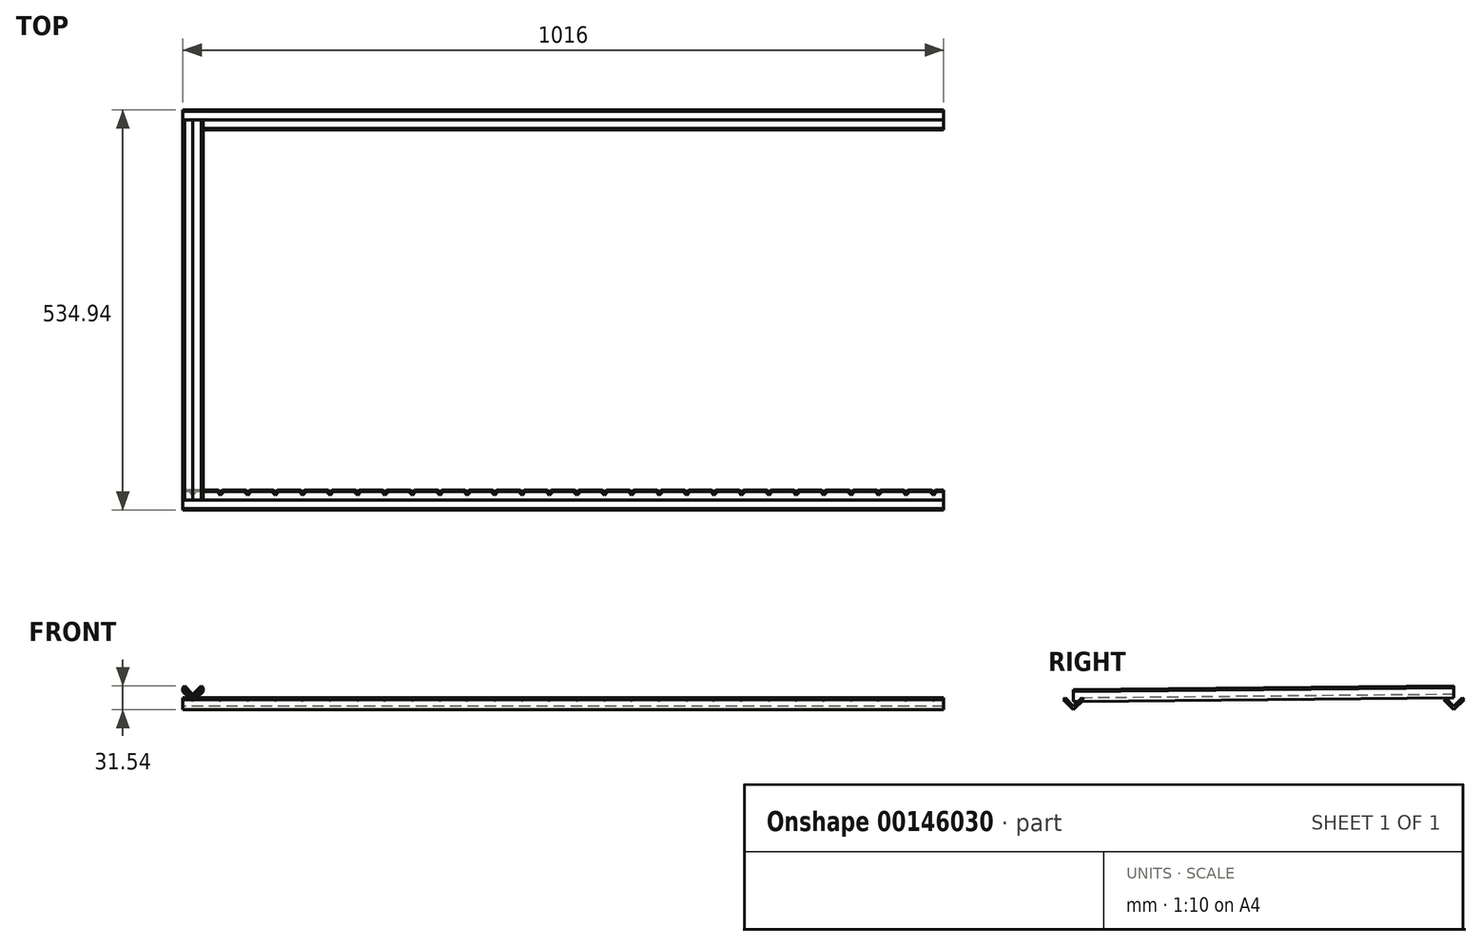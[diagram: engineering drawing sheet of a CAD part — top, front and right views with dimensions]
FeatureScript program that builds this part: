
annotation { "Feature Type Name" : "Feature", "Feature Type Description" : "" }
export const myFeature = defineFeature(function(context is Context, id is Id, definition is map)
    precondition{}
    {
        {
            var Q0;
            Q0=qCreatedBy(makeId("Right.planeOp"),FACE);
            var sketch = newSketch(context, id + "F0", { "sketchPlane" : qUnion([Q0])});
            skLineSegment(sketch, "E0", {"start": v(0, 0) * mm, "end": v(13.47, 13.47) * mm});
            skLineSegment(sketch, "E1", {"start": v(0, 0) * mm, "end": v(-13.47, 13.47) * mm});
            skLineSegment(sketch, "E2.0", {"start": v(0, 4.5) * mm, "end": v(-11.23, 15.72) * mm});
            skLineSegment(sketch, "E2.1", {"start": v(0, 4.5) * mm, "end": v(11.23, 15.72) * mm});
            skLineSegment(sketch, "E3", {"start": v(-13.47, 13.47) * mm, "end": v(-11.23, 15.72) * mm});
            skLineSegment(sketch, "E4", {"start": v(11.23, 15.72) * mm, "end": v(13.47, 13.47) * mm});
            skSolve(sketch);
        }
        {
            var Q0;
            Q0 = qSketchRegion(id + "F0", true);
            extrude(context, id + "F1", {"entities" : qUnion([Q0]), "depth" : 1016 * mm});
        }
        {
            var Q0;
            Q0=makeQuery(id+"F1.opExtrude","SWEPT_BODY",BODY,{"disambiguationData":[OSD([sQuery(id+"F0.wireOp",EDGE,"E0"),sQuery(id+"F0.wireOp",EDGE,"E1"),sQuery(id+"F0.wireOp",EDGE,"E2.0"),sQuery(id+"F0.wireOp",EDGE,"E2.1"),sQuery(id+"F0.wireOp",EDGE,"E3"),sQuery(id+"F0.wireOp",EDGE,"E4")])]});
            transform(context, id + "F2", {"entities" : qUnion([Q0]), "transformType" : TransformType.TRANSLATION_3D, "dx" : 0 * mm, "dy" : 508 * mm, "dz" : 0 * mm, "makeCopy" : true});
        }
        {
            var Q0;
            Q0=qCreatedBy(makeId("Front.planeOp"),FACE);
            var sketch = newSketch(context, id + "F3", { "sketchPlane" : qUnion([Q0])});
            skLineSegment(sketch, "E5.0", {"start": v(1016, 15.72) * mm, "end": v(0, 15.72) * mm});
            skLineSegment(sketch, "E6", {"start": v(13.47, 10.95) * mm, "end": v(26.94, 24.42) * mm});
            skLineSegment(sketch, "E7", {"start": v(13.47, 10.95) * mm, "end": v(0, 24.42) * mm});
            skLineSegment(sketch, "E8", {"start": v(0, 24.42) * mm, "end": v(2.25, 26.67) * mm});
            skLineSegment(sketch, "E9", {"start": v(24.7, 26.67) * mm, "end": v(26.94, 24.42) * mm});
            skPoint(sketch, "E10.endSnap0", {"position": v(1.12, 25.55) * mm});
            skLineSegment(sketch, "E11", {"start": v(2.25, 26.67) * mm, "end": v(24.7, 26.67) * mm});
            skLineSegment(sketch, "E12.1.0.0", {"start": v(38.87, 26.67) * mm, "end": v(61.32, 26.67) * mm});
            skPoint(sketch, "E12.1.0.1", {"position": v(37.75, 25.55) * mm});
            skLineSegment(sketch, "E12.1.0.2", {"start": v(50.1, 10.95) * mm, "end": v(36.63, 24.42) * mm});
            skLineSegment(sketch, "E12.1.0.3", {"start": v(50.1, 10.95) * mm, "end": v(63.57, 24.42) * mm});
            skLineSegment(sketch, "E12.1.0.4", {"start": v(61.32, 26.67) * mm, "end": v(63.57, 24.42) * mm});
            skLineSegment(sketch, "E12.1.0.5", {"start": v(36.63, 24.42) * mm, "end": v(38.87, 26.67) * mm});
            skLineSegment(sketch, "E12.2.0.0", {"start": v(75.5, 26.67) * mm, "end": v(97.95, 26.67) * mm});
            skPoint(sketch, "E12.2.0.1", {"position": v(74.38, 25.55) * mm});
            skLineSegment(sketch, "E12.2.0.2", {"start": v(86.72, 10.95) * mm, "end": v(73.25, 24.42) * mm});
            skLineSegment(sketch, "E12.2.0.3", {"start": v(86.72, 10.95) * mm, "end": v(100.2, 24.42) * mm});
            skLineSegment(sketch, "E12.2.0.4", {"start": v(97.95, 26.67) * mm, "end": v(100.2, 24.42) * mm});
            skLineSegment(sketch, "E12.2.0.5", {"start": v(73.25, 24.42) * mm, "end": v(75.5, 26.67) * mm});
            skLineSegment(sketch, "E12.direction1", {"start": v(13.47, 10.95) * mm, "end": v(50.1, 10.95) * mm, "construction": true});
            skLineSegment(sketch, "E13.0.3.0", {"start": v(112.13, 26.67) * mm, "end": v(134.58, 26.67) * mm});
            skPoint(sketch, "E13.3.3.0", {"position": v(111, 25.55) * mm});
            skLineSegment(sketch, "E13.4.3.0", {"start": v(123.35, 10.95) * mm, "end": v(109.88, 24.42) * mm});
            skLineSegment(sketch, "E13.7.3.0", {"start": v(123.35, 10.95) * mm, "end": v(136.82, 24.42) * mm});
            skLineSegment(sketch, "E13.10.3.0", {"start": v(134.58, 26.67) * mm, "end": v(136.82, 24.42) * mm});
            skLineSegment(sketch, "E13.13.3.0", {"start": v(109.88, 24.42) * mm, "end": v(112.13, 26.67) * mm});
            skLineSegment(sketch, "E13.0.4.0", {"start": v(148.75, 26.67) * mm, "end": v(171.2, 26.67) * mm});
            skPoint(sketch, "E13.3.4.0", {"position": v(147.63, 25.55) * mm});
            skLineSegment(sketch, "E13.4.4.0", {"start": v(159.98, 10.95) * mm, "end": v(146.5, 24.42) * mm});
            skLineSegment(sketch, "E13.7.4.0", {"start": v(159.98, 10.95) * mm, "end": v(173.45, 24.42) * mm});
            skLineSegment(sketch, "E13.10.4.0", {"start": v(171.2, 26.67) * mm, "end": v(173.45, 24.42) * mm});
            skLineSegment(sketch, "E13.13.4.0", {"start": v(146.5, 24.42) * mm, "end": v(148.75, 26.67) * mm});
            skLineSegment(sketch, "E13.0.5.0", {"start": v(185.38, 26.67) * mm, "end": v(207.83, 26.67) * mm});
            skPoint(sketch, "E13.3.5.0", {"position": v(184.26, 25.55) * mm});
            skLineSegment(sketch, "E13.4.5.0", {"start": v(196.6, 10.95) * mm, "end": v(183.13, 24.42) * mm});
            skLineSegment(sketch, "E13.7.5.0", {"start": v(196.6, 10.95) * mm, "end": v(210.08, 24.42) * mm});
            skLineSegment(sketch, "E13.10.5.0", {"start": v(207.83, 26.67) * mm, "end": v(210.08, 24.42) * mm});
            skLineSegment(sketch, "E13.13.5.0", {"start": v(183.13, 24.42) * mm, "end": v(185.38, 26.67) * mm});
            skLineSegment(sketch, "E13.0.6.0", {"start": v(222, 26.67) * mm, "end": v(244.46, 26.67) * mm});
            skPoint(sketch, "E13.3.6.0", {"position": v(220.88, 25.55) * mm});
            skLineSegment(sketch, "E13.4.6.0", {"start": v(233.23, 10.95) * mm, "end": v(219.76, 24.42) * mm});
            skLineSegment(sketch, "E13.7.6.0", {"start": v(233.23, 10.95) * mm, "end": v(246.7, 24.42) * mm});
            skLineSegment(sketch, "E13.10.6.0", {"start": v(244.46, 26.67) * mm, "end": v(246.7, 24.42) * mm});
            skLineSegment(sketch, "E13.13.6.0", {"start": v(219.76, 24.42) * mm, "end": v(222, 26.67) * mm});
            skLineSegment(sketch, "E13.0.7.0", {"start": v(258.63, 26.67) * mm, "end": v(281.08, 26.67) * mm});
            skPoint(sketch, "E13.3.7.0", {"position": v(257.51, 25.55) * mm});
            skLineSegment(sketch, "E13.4.7.0", {"start": v(269.86, 10.95) * mm, "end": v(256.39, 24.42) * mm});
            skLineSegment(sketch, "E13.7.7.0", {"start": v(269.86, 10.95) * mm, "end": v(283.33, 24.42) * mm});
            skLineSegment(sketch, "E13.10.7.0", {"start": v(281.08, 26.67) * mm, "end": v(283.33, 24.42) * mm});
            skLineSegment(sketch, "E13.13.7.0", {"start": v(256.39, 24.42) * mm, "end": v(258.63, 26.67) * mm});
            skLineSegment(sketch, "E13.0.8.0", {"start": v(295.26, 26.67) * mm, "end": v(317.71, 26.67) * mm});
            skPoint(sketch, "E13.3.8.0", {"position": v(294.14, 25.55) * mm});
            skLineSegment(sketch, "E13.4.8.0", {"start": v(306.49, 10.95) * mm, "end": v(293.01, 24.42) * mm});
            skLineSegment(sketch, "E13.7.8.0", {"start": v(306.49, 10.95) * mm, "end": v(319.96, 24.42) * mm});
            skLineSegment(sketch, "E13.10.8.0", {"start": v(317.71, 26.67) * mm, "end": v(319.96, 24.42) * mm});
            skLineSegment(sketch, "E13.13.8.0", {"start": v(293.01, 24.42) * mm, "end": v(295.26, 26.67) * mm});
            skLineSegment(sketch, "E13.0.9.0", {"start": v(331.89, 26.67) * mm, "end": v(354.34, 26.67) * mm});
            skPoint(sketch, "E13.3.9.0", {"position": v(330.76, 25.55) * mm});
            skLineSegment(sketch, "E13.4.9.0", {"start": v(343.11, 10.95) * mm, "end": v(329.64, 24.42) * mm});
            skLineSegment(sketch, "E13.7.9.0", {"start": v(343.11, 10.95) * mm, "end": v(356.58, 24.42) * mm});
            skLineSegment(sketch, "E13.10.9.0", {"start": v(354.34, 26.67) * mm, "end": v(356.58, 24.42) * mm});
            skLineSegment(sketch, "E13.13.9.0", {"start": v(329.64, 24.42) * mm, "end": v(331.89, 26.67) * mm});
            skLineSegment(sketch, "E13.0.10.0", {"start": v(368.51, 26.67) * mm, "end": v(390.96, 26.67) * mm});
            skPoint(sketch, "E13.3.10.0", {"position": v(367.4, 25.55) * mm});
            skLineSegment(sketch, "E13.4.10.0", {"start": v(379.74, 10.95) * mm, "end": v(366.27, 24.42) * mm});
            skLineSegment(sketch, "E13.7.10.0", {"start": v(379.74, 10.95) * mm, "end": v(393.2, 24.42) * mm});
            skLineSegment(sketch, "E13.10.10.0", {"start": v(390.96, 26.67) * mm, "end": v(393.2, 24.42) * mm});
            skLineSegment(sketch, "E13.13.10.0", {"start": v(366.27, 24.42) * mm, "end": v(368.51, 26.67) * mm});
            skLineSegment(sketch, "E13.0.11.0", {"start": v(405.14, 26.67) * mm, "end": v(427.6, 26.67) * mm});
            skPoint(sketch, "E13.3.11.0", {"position": v(404.02, 25.55) * mm});
            skLineSegment(sketch, "E13.4.11.0", {"start": v(416.37, 10.95) * mm, "end": v(402.9, 24.42) * mm});
            skLineSegment(sketch, "E13.7.11.0", {"start": v(416.37, 10.95) * mm, "end": v(429.84, 24.42) * mm});
            skLineSegment(sketch, "E13.10.11.0", {"start": v(427.6, 26.67) * mm, "end": v(429.84, 24.42) * mm});
            skLineSegment(sketch, "E13.13.11.0", {"start": v(402.9, 24.42) * mm, "end": v(405.14, 26.67) * mm});
            skLineSegment(sketch, "E13.0.12.0", {"start": v(441.77, 26.67) * mm, "end": v(464.22, 26.67) * mm});
            skPoint(sketch, "E13.3.12.0", {"position": v(440.64, 25.55) * mm});
            skLineSegment(sketch, "E13.4.12.0", {"start": v(453, 10.95) * mm, "end": v(439.52, 24.42) * mm});
            skLineSegment(sketch, "E13.7.12.0", {"start": v(453, 10.95) * mm, "end": v(466.46, 24.42) * mm});
            skLineSegment(sketch, "E13.10.12.0", {"start": v(464.22, 26.67) * mm, "end": v(466.46, 24.42) * mm});
            skLineSegment(sketch, "E13.13.12.0", {"start": v(439.52, 24.42) * mm, "end": v(441.77, 26.67) * mm});
            skLineSegment(sketch, "E13.0.13.0", {"start": v(478.4, 26.67) * mm, "end": v(500.84, 26.67) * mm});
            skPoint(sketch, "E13.3.13.0", {"position": v(477.27, 25.55) * mm});
            skLineSegment(sketch, "E13.4.13.0", {"start": v(489.62, 10.95) * mm, "end": v(476.15, 24.42) * mm});
            skLineSegment(sketch, "E13.7.13.0", {"start": v(489.62, 10.95) * mm, "end": v(503.09, 24.42) * mm});
            skLineSegment(sketch, "E13.10.13.0", {"start": v(500.84, 26.67) * mm, "end": v(503.09, 24.42) * mm});
            skLineSegment(sketch, "E13.13.13.0", {"start": v(476.15, 24.42) * mm, "end": v(478.4, 26.67) * mm});
            skLineSegment(sketch, "E13.0.14.0", {"start": v(515.02, 26.67) * mm, "end": v(537.47, 26.67) * mm});
            skPoint(sketch, "E13.3.14.0", {"position": v(513.9, 25.55) * mm});
            skLineSegment(sketch, "E13.4.14.0", {"start": v(526.25, 10.95) * mm, "end": v(512.78, 24.42) * mm});
            skLineSegment(sketch, "E13.7.14.0", {"start": v(526.25, 10.95) * mm, "end": v(539.72, 24.42) * mm});
            skLineSegment(sketch, "E13.10.14.0", {"start": v(537.47, 26.67) * mm, "end": v(539.72, 24.42) * mm});
            skLineSegment(sketch, "E13.13.14.0", {"start": v(512.78, 24.42) * mm, "end": v(515.02, 26.67) * mm});
            skLineSegment(sketch, "E13.0.15.0", {"start": v(551.65, 26.67) * mm, "end": v(574.1, 26.67) * mm});
            skPoint(sketch, "E13.3.15.0", {"position": v(550.53, 25.55) * mm});
            skLineSegment(sketch, "E13.4.15.0", {"start": v(562.87, 10.95) * mm, "end": v(549.4, 24.42) * mm});
            skLineSegment(sketch, "E13.7.15.0", {"start": v(562.87, 10.95) * mm, "end": v(576.34, 24.42) * mm});
            skLineSegment(sketch, "E13.10.15.0", {"start": v(574.1, 26.67) * mm, "end": v(576.34, 24.42) * mm});
            skLineSegment(sketch, "E13.13.15.0", {"start": v(549.4, 24.42) * mm, "end": v(551.65, 26.67) * mm});
            skLineSegment(sketch, "E13.0.16.0", {"start": v(588.27, 26.67) * mm, "end": v(610.73, 26.67) * mm});
            skPoint(sketch, "E13.3.16.0", {"position": v(587.15, 25.55) * mm});
            skLineSegment(sketch, "E13.4.16.0", {"start": v(599.5, 10.95) * mm, "end": v(586.03, 24.42) * mm});
            skLineSegment(sketch, "E13.7.16.0", {"start": v(599.5, 10.95) * mm, "end": v(612.97, 24.42) * mm});
            skLineSegment(sketch, "E13.10.16.0", {"start": v(610.73, 26.67) * mm, "end": v(612.97, 24.42) * mm});
            skLineSegment(sketch, "E13.13.16.0", {"start": v(586.03, 24.42) * mm, "end": v(588.27, 26.67) * mm});
            skLineSegment(sketch, "E13.0.17.0", {"start": v(624.9, 26.67) * mm, "end": v(647.35, 26.67) * mm});
            skPoint(sketch, "E13.3.17.0", {"position": v(623.78, 25.55) * mm});
            skLineSegment(sketch, "E13.4.17.0", {"start": v(636.13, 10.95) * mm, "end": v(622.66, 24.42) * mm});
            skLineSegment(sketch, "E13.7.17.0", {"start": v(636.13, 10.95) * mm, "end": v(649.6, 24.42) * mm});
            skLineSegment(sketch, "E13.10.17.0", {"start": v(647.35, 26.67) * mm, "end": v(649.6, 24.42) * mm});
            skLineSegment(sketch, "E13.13.17.0", {"start": v(622.66, 24.42) * mm, "end": v(624.9, 26.67) * mm});
            skLineSegment(sketch, "E13.0.18.0", {"start": v(661.53, 26.67) * mm, "end": v(683.98, 26.67) * mm});
            skPoint(sketch, "E13.3.18.0", {"position": v(660.4, 25.55) * mm});
            skLineSegment(sketch, "E13.4.18.0", {"start": v(672.75, 10.95) * mm, "end": v(659.28, 24.42) * mm});
            skLineSegment(sketch, "E13.7.18.0", {"start": v(672.75, 10.95) * mm, "end": v(686.22, 24.42) * mm});
            skLineSegment(sketch, "E13.10.18.0", {"start": v(683.98, 26.67) * mm, "end": v(686.22, 24.42) * mm});
            skLineSegment(sketch, "E13.13.18.0", {"start": v(659.28, 24.42) * mm, "end": v(661.53, 26.67) * mm});
            skLineSegment(sketch, "E13.0.19.0", {"start": v(698.15, 26.67) * mm, "end": v(720.6, 26.67) * mm});
            skPoint(sketch, "E13.3.19.0", {"position": v(697.03, 25.55) * mm});
            skLineSegment(sketch, "E13.4.19.0", {"start": v(709.38, 10.95) * mm, "end": v(695.9, 24.42) * mm});
            skLineSegment(sketch, "E13.7.19.0", {"start": v(709.38, 10.95) * mm, "end": v(722.85, 24.42) * mm});
            skLineSegment(sketch, "E13.10.19.0", {"start": v(720.6, 26.67) * mm, "end": v(722.85, 24.42) * mm});
            skLineSegment(sketch, "E13.13.19.0", {"start": v(695.9, 24.42) * mm, "end": v(698.15, 26.67) * mm});
            skLineSegment(sketch, "E14.0.20.0", {"start": v(734.78, 26.67) * mm, "end": v(757.23, 26.67) * mm});
            skPoint(sketch, "E14.3.20.0", {"position": v(733.66, 25.55) * mm});
            skLineSegment(sketch, "E14.4.20.0", {"start": v(746, 10.95) * mm, "end": v(732.54, 24.42) * mm});
            skLineSegment(sketch, "E14.7.20.0", {"start": v(746, 10.95) * mm, "end": v(759.48, 24.42) * mm});
            skLineSegment(sketch, "E14.10.20.0", {"start": v(757.23, 26.67) * mm, "end": v(759.48, 24.42) * mm});
            skLineSegment(sketch, "E14.13.20.0", {"start": v(732.54, 24.42) * mm, "end": v(734.78, 26.67) * mm});
            skLineSegment(sketch, "E14.0.21.0", {"start": v(771.4, 26.67) * mm, "end": v(793.86, 26.67) * mm});
            skPoint(sketch, "E14.3.21.0", {"position": v(770.29, 25.55) * mm});
            skLineSegment(sketch, "E14.4.21.0", {"start": v(782.63, 10.95) * mm, "end": v(769.16, 24.42) * mm});
            skLineSegment(sketch, "E14.7.21.0", {"start": v(782.63, 10.95) * mm, "end": v(796.1, 24.42) * mm});
            skLineSegment(sketch, "E14.10.21.0", {"start": v(793.86, 26.67) * mm, "end": v(796.1, 24.42) * mm});
            skLineSegment(sketch, "E14.13.21.0", {"start": v(769.16, 24.42) * mm, "end": v(771.4, 26.67) * mm});
            skLineSegment(sketch, "E14.0.22.0", {"start": v(808.04, 26.67) * mm, "end": v(830.49, 26.67) * mm});
            skPoint(sketch, "E14.3.22.0", {"position": v(806.91, 25.55) * mm});
            skLineSegment(sketch, "E14.4.22.0", {"start": v(819.26, 10.95) * mm, "end": v(805.8, 24.42) * mm});
            skLineSegment(sketch, "E14.7.22.0", {"start": v(819.26, 10.95) * mm, "end": v(832.73, 24.42) * mm});
            skLineSegment(sketch, "E14.10.22.0", {"start": v(830.49, 26.67) * mm, "end": v(832.73, 24.42) * mm});
            skLineSegment(sketch, "E14.13.22.0", {"start": v(805.8, 24.42) * mm, "end": v(808.04, 26.67) * mm});
            skLineSegment(sketch, "E14.0.23.0", {"start": v(844.66, 26.67) * mm, "end": v(867.11, 26.67) * mm});
            skPoint(sketch, "E14.3.23.0", {"position": v(843.54, 25.55) * mm});
            skLineSegment(sketch, "E14.4.23.0", {"start": v(855.89, 10.95) * mm, "end": v(842.42, 24.42) * mm});
            skLineSegment(sketch, "E14.7.23.0", {"start": v(855.89, 10.95) * mm, "end": v(869.36, 24.42) * mm});
            skLineSegment(sketch, "E14.10.23.0", {"start": v(867.11, 26.67) * mm, "end": v(869.36, 24.42) * mm});
            skLineSegment(sketch, "E14.13.23.0", {"start": v(842.42, 24.42) * mm, "end": v(844.66, 26.67) * mm});
            skLineSegment(sketch, "E14.0.24.0", {"start": v(881.29, 26.67) * mm, "end": v(903.74, 26.67) * mm});
            skPoint(sketch, "E14.3.24.0", {"position": v(880.17, 25.55) * mm});
            skLineSegment(sketch, "E14.4.24.0", {"start": v(892.51, 10.95) * mm, "end": v(879.04, 24.42) * mm});
            skLineSegment(sketch, "E14.7.24.0", {"start": v(892.51, 10.95) * mm, "end": v(905.98, 24.42) * mm});
            skLineSegment(sketch, "E14.10.24.0", {"start": v(903.74, 26.67) * mm, "end": v(905.98, 24.42) * mm});
            skLineSegment(sketch, "E14.13.24.0", {"start": v(879.04, 24.42) * mm, "end": v(881.29, 26.67) * mm});
            skLineSegment(sketch, "E14.0.25.0", {"start": v(917.92, 26.67) * mm, "end": v(940.37, 26.67) * mm});
            skPoint(sketch, "E14.3.25.0", {"position": v(916.8, 25.55) * mm});
            skLineSegment(sketch, "E14.4.25.0", {"start": v(929.14, 10.95) * mm, "end": v(915.67, 24.42) * mm});
            skLineSegment(sketch, "E14.7.25.0", {"start": v(929.14, 10.95) * mm, "end": v(942.61, 24.42) * mm});
            skLineSegment(sketch, "E14.10.25.0", {"start": v(940.37, 26.67) * mm, "end": v(942.61, 24.42) * mm});
            skLineSegment(sketch, "E14.13.25.0", {"start": v(915.67, 24.42) * mm, "end": v(917.92, 26.67) * mm});
            skLineSegment(sketch, "E14.0.26.0", {"start": v(954.54, 26.67) * mm, "end": v(977, 26.67) * mm});
            skPoint(sketch, "E14.3.26.0", {"position": v(953.42, 25.55) * mm});
            skLineSegment(sketch, "E14.4.26.0", {"start": v(965.77, 10.95) * mm, "end": v(952.3, 24.42) * mm});
            skLineSegment(sketch, "E14.7.26.0", {"start": v(965.77, 10.95) * mm, "end": v(979.24, 24.42) * mm});
            skLineSegment(sketch, "E14.10.26.0", {"start": v(977, 26.67) * mm, "end": v(979.24, 24.42) * mm});
            skLineSegment(sketch, "E14.13.26.0", {"start": v(952.3, 24.42) * mm, "end": v(954.54, 26.67) * mm});
            skLineSegment(sketch, "E14.0.27.0", {"start": v(991.17, 26.67) * mm, "end": v(1013.62, 26.67) * mm});
            skPoint(sketch, "E14.3.27.0", {"position": v(990.05, 25.55) * mm});
            skLineSegment(sketch, "E14.4.27.0", {"start": v(1002.4, 10.95) * mm, "end": v(988.92, 24.42) * mm});
            skLineSegment(sketch, "E14.7.27.0", {"start": v(1002.4, 10.95) * mm, "end": v(1015.86, 24.42) * mm});
            skLineSegment(sketch, "E14.10.27.0", {"start": v(1013.62, 26.67) * mm, "end": v(1015.86, 24.42) * mm});
            skLineSegment(sketch, "E14.13.27.0", {"start": v(988.92, 24.42) * mm, "end": v(991.17, 26.67) * mm});
            skSolve(sketch);
        }
        {
            var Q0;
            Q0 = qSketchRegion(id + "F3", true);
            extrude(context, id + "F4", {"entities" : qUnion([Q0]), "operationType" : NewBodyOperationType.REMOVE, "oppositeDirection" : true, "depth" : 25.4 * mm});
        }
        {
            var Q0;
            Q0=qCreatedBy(makeId("Right.planeOp"),FACE);
            cPlane(context, id + "F5", {"entities" : qUnion([Q0]), "cplaneType" : CPlaneType.OFFSET, "offset" : 13.47 * mm, "width" : 152.4 * mm, "height" : 152.4 * mm});
        }
        {
            var Q0;
            Q0=qCreatedBy(id+"F5.planeOp",FACE);
            var sketch = newSketch(context, id + "F6", { "sketchPlane" : qUnion([Q0])});
            skLineSegment(sketch, "E15.0", {"start": v(494.53, 13.47) * mm, "end": v(496.77, 15.72) * mm});
            skLineSegment(sketch, "E16.0", {"start": v(508, 4.5) * mm, "end": v(496.77, 15.72) * mm});
            skLineSegment(sketch, "E17.0", {"start": v(6.46, 10.95) * mm, "end": v(11.23, 15.72) * mm, "construction": true});
            skLineSegment(sketch, "E18", {"start": v(6.46, 10.95) * mm, "end": v(496.77, 15.72) * mm, "construction": true});
            skLineSegment(sketch, "E19", {"start": v(6.46, 10.95) * mm, "end": v(0, 10.95) * mm, "construction": true});
            skSolve(sketch);
        }
        {
            var Q0;
            Q0=sQuery(id+"F6.wireOp",EDGE,"E18");
            var Q1;
            Q1=sQuery(id+"F6.wireOp",VERTEX,"E19.end");
            cPlane(context, id + "F7", {"entities" : qUnion([Q0, Q1]), "cplaneType" : CPlaneType.LINE_POINT, "offset" : 25.4 * mm, "width" : 152.4 * mm, "height" : 152.4 * mm});
        }
        {
            var Q0;
            Q0=qCreatedBy(id+"F7.planeOp",FACE);
            var sketch = newSketch(context, id + "F8", { "sketchPlane" : qUnion([Q0])});
            skLineSegment(sketch, "E20.0", {"start": v(-13.47, 10.89) * mm, "end": v(-8.7, 15.6) * mm, "construction": true});
            skLineSegment(sketch, "E21", {"start": v(-13.47, 10.89) * mm, "end": v(0, 24.36) * mm});
            skLineSegment(sketch, "E22", {"start": v(-13.47, 10.89) * mm, "end": v(-26.94, 24.36) * mm});
            skLineSegment(sketch, "E23.0", {"start": v(-13.47, 15.38) * mm, "end": v(-24.7, 26.6) * mm});
            skLineSegment(sketch, "E23.1", {"start": v(-13.47, 15.38) * mm, "end": v(-2.25, 26.6) * mm});
            skLineSegment(sketch, "E24", {"start": v(-26.94, 24.36) * mm, "end": v(-24.7, 26.6) * mm});
            skLineSegment(sketch, "E25", {"start": v(-2.25, 26.6) * mm, "end": v(0, 24.36) * mm});
            skSolve(sketch);
        }
        {
            var Q0;
            Q0 = qSketchRegion(id + "F8", true);
            extrude(context, id + "F9", {"entities" : qUnion([Q0]), "depth" : 508 * mm});
        }
    });
